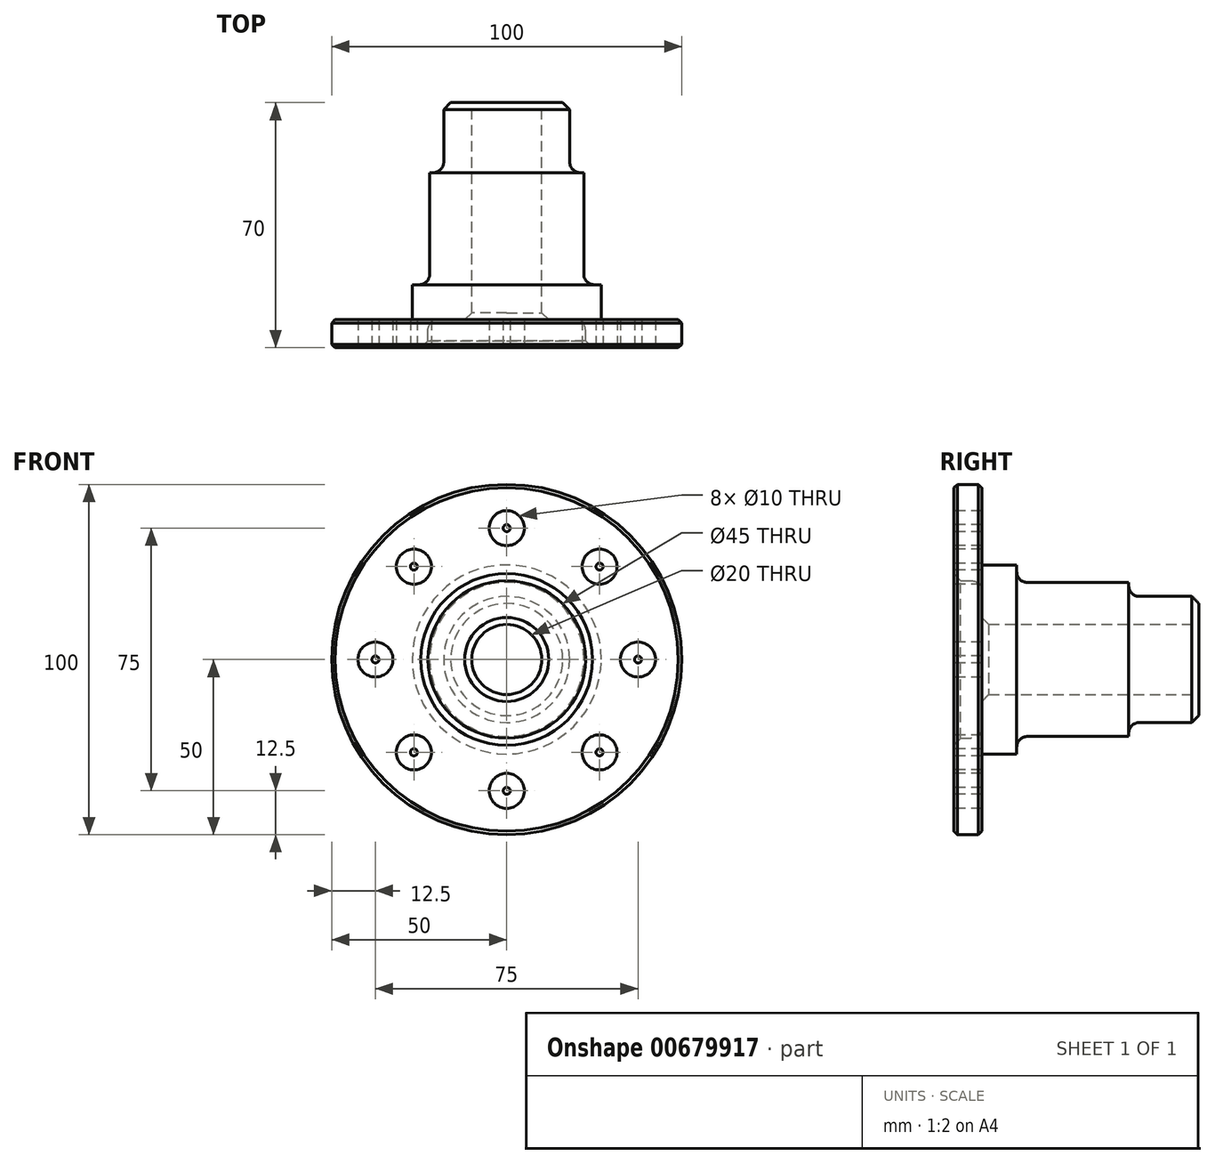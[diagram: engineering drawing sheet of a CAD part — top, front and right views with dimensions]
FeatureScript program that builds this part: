
annotation { "Feature Type Name" : "Feature", "Feature Type Description" : "" }
export const myFeature = defineFeature(function(context is Context, id is Id, definition is map)
    precondition{}
    {
        {
            var Q0;
            Q0=qCreatedBy(makeId("Right.planeOp"),FACE);
            var sketch = newSketch(context, id + "F0", { "sketchPlane" : qUnion([Q0])});
            skLineSegment(sketch, "E0", {"start": v(0, 0) * mm, "end": v(-26.56, 0) * mm, "construction": true});
            skLineSegment(sketch, "E1", {"start": v(0, 22.5) * mm, "end": v(8, 22.5) * mm});
            skLineSegment(sketch, "E2", {"start": v(8, 22.5) * mm, "end": v(8, 10) * mm});
            skLineSegment(sketch, "E3", {"start": v(8, 10) * mm, "end": v(70, 10) * mm});
            skLineSegment(sketch, "E4", {"start": v(70, 10) * mm, "end": v(70, 18) * mm});
            skLineSegment(sketch, "E5", {"start": v(70, 18) * mm, "end": v(50, 18) * mm});
            skLineSegment(sketch, "E6", {"start": v(50, 18) * mm, "end": v(50, 22) * mm});
            skLineSegment(sketch, "E7", {"start": v(50, 22) * mm, "end": v(18, 22) * mm});
            skLineSegment(sketch, "E8", {"start": v(18, 22) * mm, "end": v(18, 27) * mm});
            skLineSegment(sketch, "E9", {"start": v(18, 27) * mm, "end": v(8, 27) * mm});
            skLineSegment(sketch, "E10", {"start": v(8, 27) * mm, "end": v(8, 50) * mm});
            skLineSegment(sketch, "E11", {"start": v(8, 50) * mm, "end": v(0, 50) * mm});
            skLineSegment(sketch, "E12", {"start": v(0, 50) * mm, "end": v(0, 22.5) * mm});
            skSolve(sketch);
        }
        {
            var Q0;
            Q0=qSketchRegion(id+"F0",true);
            var Q1;
            Q1=sQuery(id+"F0.wireOp",EDGE,"E0");
            revolve(context, id + "F1", {"entities" : qUnion([Q0]), "axis" : qUnion([Q1]), "revolveType" : RevolveType.FULL});
        }
        {
            var Q0;
            Q0=makeQuery(id+"F1.opRevolve","SWEPT_FACE",FACE,{"disambiguationData":[OSD([sQuery(id+"F0.wireOp",EDGE,"E12")])]});
            var sketch = newSketch(context, id + "F2", { "sketchPlane" : qUnion([Q0])});
            skCircle(sketch, "E13", {"center": v(0, -37.5) * mm, "radius": 5 * mm});
            skCircle(sketch, "E14.1.0", {"center": v(26.52, -26.52) * mm, "radius": 5 * mm});
            skCircle(sketch, "E14.2.0", {"center": v(37.5, 0) * mm, "radius": 5 * mm});
            skCircle(sketch, "E14.3.0", {"center": v(26.52, 26.52) * mm, "radius": 5 * mm});
            skCircle(sketch, "E14.4.0", {"center": v(0, 37.5) * mm, "radius": 5 * mm});
            skCircle(sketch, "E14.5.0", {"center": v(-26.52, 26.52) * mm, "radius": 5 * mm});
            skCircle(sketch, "E14.6.0", {"center": v(-37.5, 0) * mm, "radius": 5 * mm});
            skCircle(sketch, "E14.7.0", {"center": v(-26.52, -26.52) * mm, "radius": 5 * mm});
            skPoint(sketch, "E14.center", {"position": v(0, 0) * mm});
            skCircle(sketch, "E15", {"center": v(0, 0) * mm, "radius": 37.5 * mm, "construction": true});
            skLineSegment(sketch, "E16", {"start": v(0, 0) * mm, "end": v(76.08, 0) * mm, "construction": true});
            skLineSegment(sketch, "E17", {"start": v(0, 0) * mm, "end": v(0, 57.53) * mm, "construction": true});
            skLineSegment(sketch, "E18", {"start": v(0, 0) * mm, "end": v(26.52, 26.52) * mm, "construction": true});
            skLineSegment(sketch, "E19", {"start": v(26.52, 26.52) * mm, "end": v(41.54, 41.54) * mm, "construction": true});
            skSolve(sketch);
        }
        {
            var Q0;
            Q0=qSketchRegion(id+"F2",true);
            extrude(context, id + "F3", {"entities" : qUnion([Q0]), "operationType" : NewBodyOperationType.REMOVE, "endBound" : BoundingType.THROUGH_ALL, "oppositeDirection" : true, "depth" : 25 * mm, "offsetDistance" : 25 * mm});
        }
        {
            var Q0;
            Q0=makeQuery(id+"F1.opRevolve","SWEPT_EDGE",EDGE,{"disambiguationData":[OSD([sQuery(id+"F0.wireOp",EDGE,"E1"),sQuery(id+"F0.wireOp",EDGE,"E12")])]});
            var Q1;
            Q1=makeQuery(id+"F1.opRevolve","SWEPT_EDGE",EDGE,{"disambiguationData":[OSD([sQuery(id+"F0.wireOp",EDGE,"E2"),sQuery(id+"F0.wireOp",EDGE,"E3")])]});
            var Q2;
            Q2=makeQuery(id+"F1.opRevolve","SWEPT_EDGE",EDGE,{"disambiguationData":[OSD([sQuery(id+"F0.wireOp",EDGE,"E4"),sQuery(id+"F0.wireOp",EDGE,"E5")])]});
            chamfer(context, id + "F4", {"entities" : qUnion([Q0, Q1, Q2]), "width" : 2 * mm, "tangentPropagation" : true});
        }
        {
            var Q0;
            Q0=makeQuery(id+"F1.opRevolve","SWEPT_EDGE",EDGE,{"disambiguationData":[OSD([sQuery(id+"F0.wireOp",EDGE,"E1"),sQuery(id+"F0.wireOp",EDGE,"E2")])]});
            var Q1;
            Q1=makeQuery(id+"F1.opRevolve","SWEPT_EDGE",EDGE,{"disambiguationData":[OSD([sQuery(id+"F0.wireOp",EDGE,"E5"),sQuery(id+"F0.wireOp",EDGE,"E6")])]});
            var Q2;
            Q2=makeQuery(id+"F1.opRevolve","SWEPT_EDGE",EDGE,{"disambiguationData":[OSD([sQuery(id+"F0.wireOp",EDGE,"E7"),sQuery(id+"F0.wireOp",EDGE,"E8")])]});
            fillet(context, id + "F5", {"entities" : qUnion([Q0, Q1, Q2]), "radius" : 3 * mm, "tangentPropagation" : true, "allowEdgeOverflow" : false});
        }
        {
            var Q0;
            Q0=makeQuery(id+"F1.opRevolve","SWEPT_EDGE",EDGE,{"disambiguationData":[OSD([sQuery(id+"F0.wireOp",EDGE,"E11"),sQuery(id+"F0.wireOp",EDGE,"E12")])]});
            var Q1;
            Q1=makeQuery(id+"F1.opRevolve","SWEPT_EDGE",EDGE,{"disambiguationData":[OSD([sQuery(id+"F0.wireOp",EDGE,"E10"),sQuery(id+"F0.wireOp",EDGE,"E11")])]});
            chamfer(context, id + "F6", {"entities" : qUnion([Q0, Q1]), "width" : 1 * mm, "tangentPropagation" : true});
        }
        {
            var Q0;
            Q0=makeQuery(id+"F2.imprint","IMPRINT",FACE,{"disambiguationData":[TD([[makeQuery(id+"F2.imprint","IMPRINT",EDGE,{"derivedFrom":sQuery(id+"F2.wireOp",EDGE,"E13")}),-1.0]])]});
            var sketch = newSketch(context, id + "F7", { "sketchPlane" : qUnion([Q0])});
            skPoint(sketch, "E20.0", {"position": v(0, 37.5) * mm});
            skPoint(sketch, "E21.0", {"position": v(-26.52, 26.52) * mm});
            skPoint(sketch, "E22.0", {"position": v(26.52, 26.52) * mm});
            skPoint(sketch, "E23.0", {"position": v(37.5, 0) * mm});
            skPoint(sketch, "E24.0", {"position": v(26.52, -26.52) * mm});
            skPoint(sketch, "E25.0", {"position": v(0, -37.5) * mm});
            skPoint(sketch, "E26.0", {"position": v(-26.52, -26.52) * mm});
            skPoint(sketch, "E27.0", {"position": v(-37.5, 0) * mm});
            skCircle(sketch, "E28", {"center": v(0, 37.5) * mm, "radius": 1 * mm});
            skCircle(sketch, "E29.1.0", {"center": v(-26.52, 26.52) * mm, "radius": 1 * mm});
            skCircle(sketch, "E29.2.0", {"center": v(-37.5, 0) * mm, "radius": 1 * mm});
            skCircle(sketch, "E29.3.0", {"center": v(-26.52, -26.52) * mm, "radius": 1 * mm});
            skCircle(sketch, "E29.4.0", {"center": v(0, -37.5) * mm, "radius": 1 * mm});
            skCircle(sketch, "E29.5.0", {"center": v(26.52, -26.52) * mm, "radius": 1 * mm});
            skCircle(sketch, "E29.6.0", {"center": v(37.5, 0) * mm, "radius": 1 * mm});
            skCircle(sketch, "E29.7.0", {"center": v(26.52, 26.52) * mm, "radius": 1 * mm});
            skPoint(sketch, "E29.center", {"position": v(0, 0) * mm});
            skSolve(sketch);
        }
        {
            var Q0;
            Q0=qSketchRegion(id+"F7",true);
            extrude(context, id + "F8", {"entities" : qUnion([Q0]), "oppositeDirection" : true, "depth" : 8 * mm, "offsetDistance" : 25 * mm});
        }
    });
